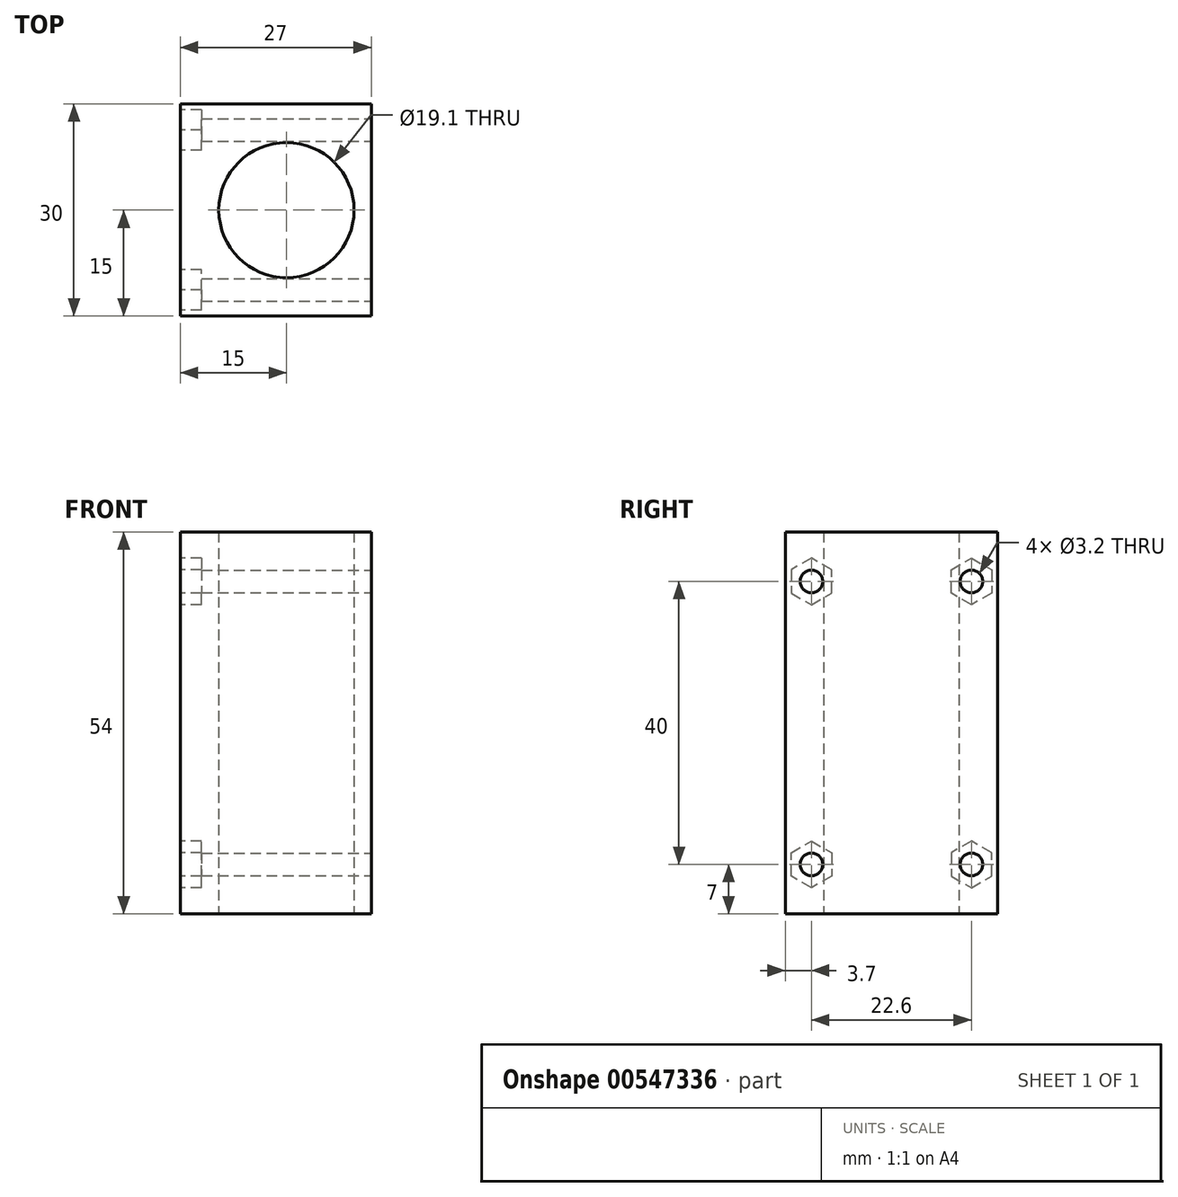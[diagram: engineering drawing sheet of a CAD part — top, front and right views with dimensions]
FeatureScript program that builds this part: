
annotation { "Feature Type Name" : "Feature", "Feature Type Description" : "" }
export const myFeature = defineFeature(function(context is Context, id is Id, definition is map)
    precondition{}
    {
        {
            var Q0;
            Q0=qCreatedBy(makeId("Top.planeOp"),FACE);
            var sketch = newSketch(context, id + "F0", { "sketchPlane" : qUnion([Q0])});
            skCircle(sketch, "E0", {"center": v(0, 0) * mm, "radius": 9.55 * mm});
            skLineSegment(sketch, "E1.bottom", {"start": v(-15, 15) * mm, "end": v(12, 15) * mm});
            skLineSegment(sketch, "E1.top", {"start": v(-15, -15) * mm, "end": v(12, -15) * mm});
            skLineSegment(sketch, "E1.left", {"start": v(-15, 15) * mm, "end": v(-15, -15) * mm});
            skLineSegment(sketch, "E1.right", {"start": v(12, 15) * mm, "end": v(12, -15) * mm});
            skSolve(sketch);
        }
        {
            var Q0;
            Q0 = qSketchRegion(id + "F0", true);
            extrude(context, id + "F1", {"entities" : qUnion([Q0]), "depth" : 54 * mm, "offsetDistance" : 25 * mm, "symmetric" : true});
        }
        {
            var Q0;
            Q0=makeQuery(id+"F1.opExtrude","SWEPT_FACE",FACE,{"disambiguationData":[OSD([sQuery(id+"F0.wireOp",EDGE,"E1.right")])]});
            var sketch = newSketch(context, id + "F2", { "sketchPlane" : qUnion([Q0])});
            skCircle(sketch, "E2", {"center": v(11.3, 20) * mm, "radius": 1.6 * mm});
            skCircle(sketch, "E3.MirrorC", {"center": v(11.3, -20) * mm, "radius": 1.6 * mm});
            skCircle(sketch, "E4.MirrorC", {"center": v(-11.3, 20) * mm, "radius": 1.6 * mm});
            skCircle(sketch, "E5.MirrorC", {"center": v(-11.3, -20) * mm, "radius": 1.6 * mm});
            skSolve(sketch);
        }
        {
            var Q0;
            Q0 = qSketchRegion(id + "F2", true);
            extrude(context, id + "F3", {"entities" : qUnion([Q0]), "operationType" : NewBodyOperationType.REMOVE, "endBound" : BoundingType.THROUGH_ALL, "oppositeDirection" : true, "depth" : 25 * mm, "offsetDistance" : 25 * mm});
        }
        {
            var Q0;
            Q0=makeQuery(id+"F1.opExtrude","SWEPT_FACE",FACE,{"disambiguationData":[OSD([sQuery(id+"F0.wireOp",EDGE,"E1.left")])]});
            var sketch = newSketch(context, id + "F4", { "sketchPlane" : qUnion([Q0])});
            skCircle(sketch, "E6.cCircle", {"center": v(-11.3, -20) * mm, "radius": 2.85 * mm, "construction": true});
            skLineSegment(sketch, "E6.0", {"start": v(-14.15, -18.35) * mm, "end": v(-11.3, -16.7) * mm});
            skLineSegment(sketch, "E6.1", {"start": v(-11.3, -16.7) * mm, "end": v(-8.45, -18.35) * mm});
            skLineSegment(sketch, "E6.2", {"start": v(-8.45, -18.35) * mm, "end": v(-8.45, -21.65) * mm});
            skLineSegment(sketch, "E6.3", {"start": v(-8.45, -21.65) * mm, "end": v(-11.3, -23.3) * mm});
            skLineSegment(sketch, "E6.4", {"start": v(-11.3, -23.3) * mm, "end": v(-14.15, -21.65) * mm});
            skLineSegment(sketch, "E6.5", {"start": v(-14.15, -21.65) * mm, "end": v(-14.15, -18.35) * mm});
            skPoint(sketch, "E6.0.midPoint", {"position": v(-12.72, -17.53) * mm});
            skLineSegment(sketch, "E7.MirrorCS", {"start": v(-8.45, 18.35) * mm, "end": v(-8.45, 21.65) * mm});
            skLineSegment(sketch, "E8.MirrorCS", {"start": v(-8.45, 21.65) * mm, "end": v(-11.3, 23.3) * mm});
            skLineSegment(sketch, "E9.MirrorCS", {"start": v(-11.3, 23.3) * mm, "end": v(-14.15, 21.65) * mm});
            skLineSegment(sketch, "E10.MirrorCS", {"start": v(-14.15, 21.65) * mm, "end": v(-14.15, 18.35) * mm});
            skLineSegment(sketch, "E11.MirrorCS", {"start": v(-14.15, 18.35) * mm, "end": v(-11.3, 16.7) * mm});
            skLineSegment(sketch, "E12.MirrorCS", {"start": v(-11.3, 16.7) * mm, "end": v(-8.45, 18.35) * mm});
            skLineSegment(sketch, "E13.MirrorCS", {"start": v(8.45, -18.35) * mm, "end": v(8.45, -21.65) * mm});
            skLineSegment(sketch, "E14.MirrorCS", {"start": v(11.3, -16.7) * mm, "end": v(8.45, -18.35) * mm});
            skLineSegment(sketch, "E15.MirrorCS", {"start": v(14.15, -18.35) * mm, "end": v(11.3, -16.7) * mm});
            skLineSegment(sketch, "E16.MirrorCS", {"start": v(14.15, -21.65) * mm, "end": v(14.15, -18.35) * mm});
            skLineSegment(sketch, "E17.MirrorCS", {"start": v(11.3, -23.3) * mm, "end": v(14.15, -21.65) * mm});
            skLineSegment(sketch, "E18.MirrorCS", {"start": v(8.45, -21.65) * mm, "end": v(11.3, -23.3) * mm});
            skLineSegment(sketch, "E19.MirrorCS", {"start": v(11.3, 16.7) * mm, "end": v(8.45, 18.35) * mm});
            skLineSegment(sketch, "E20.MirrorCS", {"start": v(14.15, 18.35) * mm, "end": v(11.3, 16.7) * mm});
            skLineSegment(sketch, "E21.MirrorCS", {"start": v(14.15, 21.65) * mm, "end": v(14.15, 18.35) * mm});
            skLineSegment(sketch, "E22.MirrorCS", {"start": v(11.3, 23.3) * mm, "end": v(14.15, 21.65) * mm});
            skLineSegment(sketch, "E23.MirrorCS", {"start": v(8.45, 21.65) * mm, "end": v(11.3, 23.3) * mm});
            skLineSegment(sketch, "E24.MirrorCS", {"start": v(8.45, 18.35) * mm, "end": v(8.45, 21.65) * mm});
            skSolve(sketch);
        }
        {
            var Q0;
            Q0 = qSketchRegion(id + "F4", true);
            extrude(context, id + "F5", {"entities" : qUnion([Q0]), "operationType" : NewBodyOperationType.REMOVE, "oppositeDirection" : true, "depth" : 3 * mm, "offsetDistance" : 25 * mm});
        }
    });
